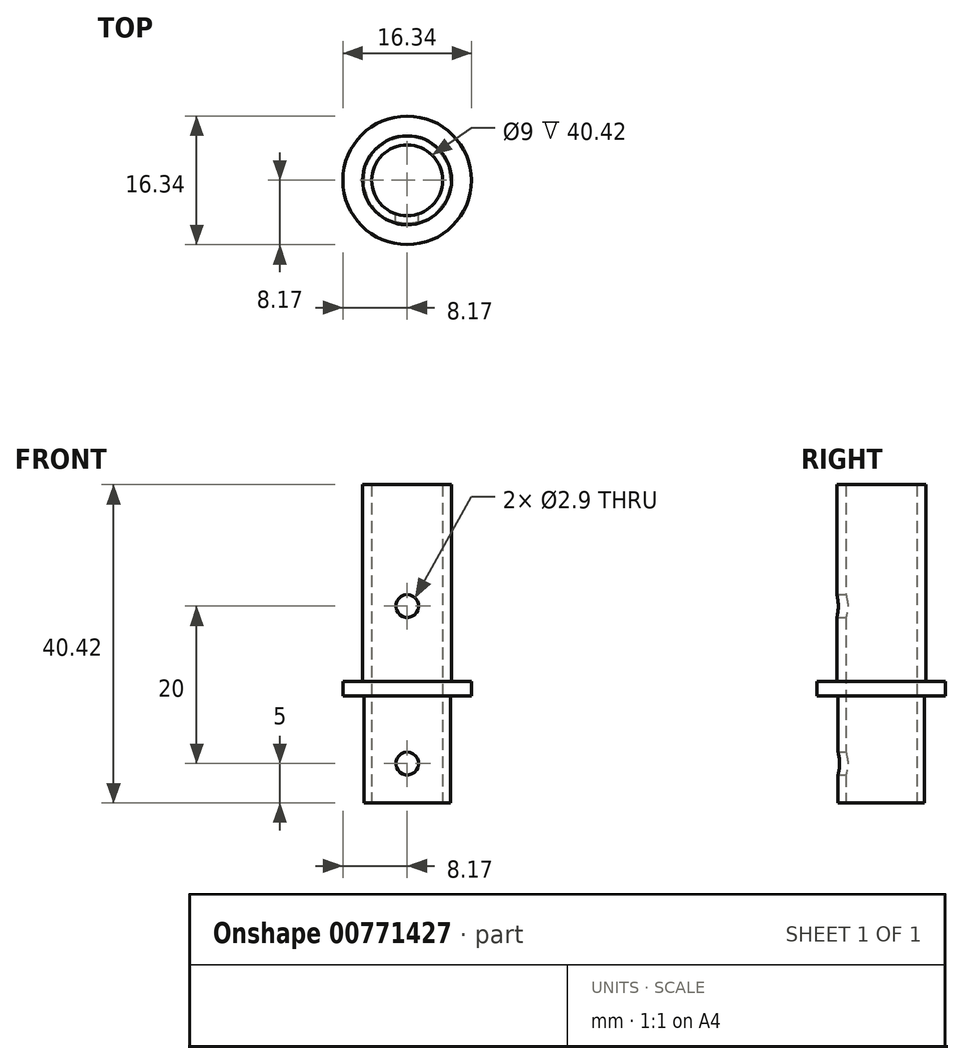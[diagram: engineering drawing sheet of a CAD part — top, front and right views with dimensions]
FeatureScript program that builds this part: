
annotation { "Feature Type Name" : "Feature", "Feature Type Description" : "" }
export const myFeature = defineFeature(function(context is Context, id is Id, definition is map)
    precondition{}
    {
        {
            var Q0;
            Q0=qCreatedBy(makeId("Top.planeOp"),FACE);
            var sketch = newSketch(context, id + "F0", { "sketchPlane" : qUnion([Q0])});
            skCircle(sketch, "E0", {"center": v(0, 0) * mm, "radius": 5.5 * mm});
            skSolve(sketch);
        }
        {
            var Q0;
            Q0 = qSketchRegion(id + "F0", true);
            extrude(context, id + "F1", {"entities" : qUnion([Q0]), "depth" : 13.6 * mm, "offsetDistance" : 25 * mm});
        }
        {
            var Q0;
            Q0=makeQuery(id+"F1.opExtrude","CAP_FACE",FACE,{"disambiguationData":[OSD([sQuery(id+"F0.wireOp",EDGE,"E0")])],"isStart":false});
            var sketch = newSketch(context, id + "F2", { "sketchPlane" : qUnion([Q0])});
            skCircle(sketch, "E1", {"center": v(0, 0) * mm, "radius": 8.16 * mm});
            skSolve(sketch);
        }
        {
            var Q0;
            Q0 = qSketchRegion(id + "F2", true);
            extrude(context, id + "F3", {"entities" : qUnion([Q0]), "operationType" : NewBodyOperationType.ADD, "depth" : 1.82 * mm, "offsetDistance" : 25 * mm});
        }
        {
            var Q0;
            Q0=makeQuery(id+"F3.opExtrude","CAP_FACE",FACE,{"disambiguationData":[OSD([sQuery(id+"F2.wireOp",EDGE,"E1")])],"isStart":false});
            var sketch = newSketch(context, id + "F4", { "sketchPlane" : qUnion([Q0])});
            skCircle(sketch, "E2", {"center": v(0, 0) * mm, "radius": 5.65 * mm});
            skSolve(sketch);
        }
        {
            var Q0;
            Q0=makeQuery(id+"F4.imprint","IMPRINT",FACE,{"disambiguationData":[TD([[makeQuery(id+"F4.imprint","IMPRINT",EDGE,{"derivedFrom":sQuery(id+"F4.wireOp",EDGE,"E2")}),1.0]])]});
            extrude(context, id + "F5", {"entities" : qUnion([Q0]), "operationType" : NewBodyOperationType.ADD, "depth" : 25 * mm, "offsetDistance" : 25 * mm});
        }
        {
            var Q0;
            Q0=makeQuery(id+"F1.opExtrude","CAP_FACE",FACE,{"disambiguationData":[OSD([sQuery(id+"F0.wireOp",EDGE,"E0")])],"isStart":true});
            var sketch = newSketch(context, id + "F6", { "sketchPlane" : qUnion([Q0])});
            skCircle(sketch, "E3", {"center": v(0, 0) * mm, "radius": 4.5 * mm});
            skSolve(sketch);
        }
        {
            var Q0;
            Q0=makeQuery(id+"F6.imprint","IMPRINT",FACE,{"disambiguationData":[TD([[makeQuery(id+"F6.imprint","IMPRINT",EDGE,{"derivedFrom":sQuery(id+"F6.wireOp",EDGE,"E3")}),1.0]])]});
            extrude(context, id + "F7", {"entities" : qUnion([Q0]), "operationType" : NewBodyOperationType.REMOVE, "endBound" : BoundingType.THROUGH_ALL, "oppositeDirection" : true, "depth" : 25 * mm, "offsetDistance" : 25 * mm});
        }
        {
            var Q0;
            Q0=qCreatedBy(makeId("Front.planeOp"),FACE);
            var sketch = newSketch(context, id + "F8", { "sketchPlane" : qUnion([Q0])});
            skCircle(sketch, "E4", {"center": v(0, 25) * mm, "radius": 1.45 * mm});
            skCircle(sketch, "E5", {"center": v(0, 5) * mm, "radius": 1.45 * mm});
            skSolve(sketch);
        }
        {
            var Q0;
            Q0 = qSketchRegion(id + "F8", true);
            extrude(context, id + "F9", {"entities" : qUnion([Q0]), "operationType" : NewBodyOperationType.REMOVE, "depth" : 12 * mm, "offsetDistance" : 25 * mm});
        }
    });
